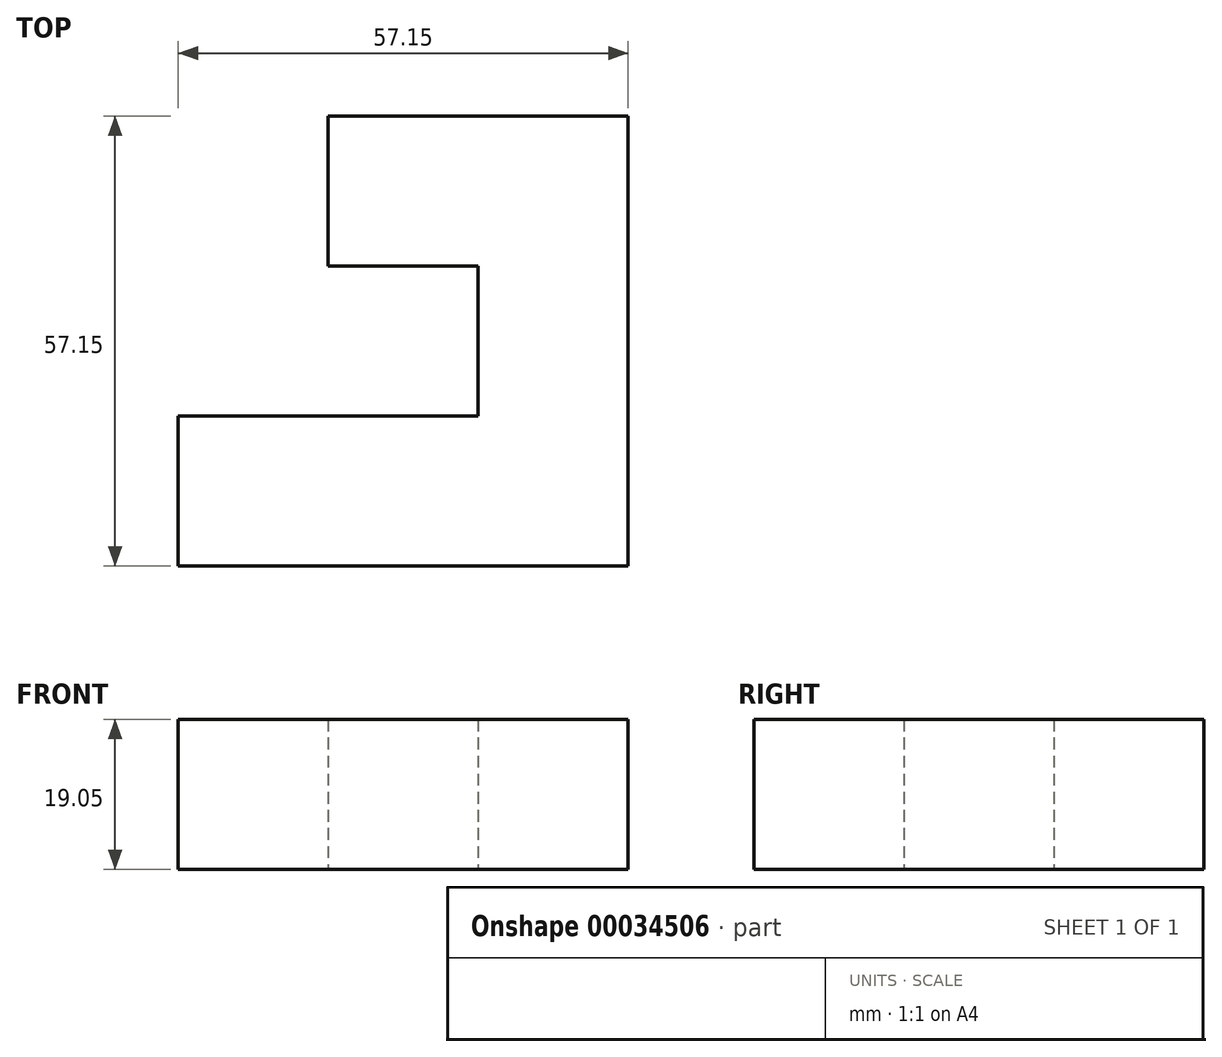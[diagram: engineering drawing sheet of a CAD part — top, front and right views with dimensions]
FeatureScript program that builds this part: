
annotation { "Feature Type Name" : "Feature", "Feature Type Description" : "" }
export const myFeature = defineFeature(function(context is Context, id is Id, definition is map)
    precondition{}
    {
        {
            var Q0;
            Q0=qCreatedBy(makeId("Top.planeOp"),FACE);
            var sketch = newSketch(context, id + "F0", { "sketchPlane" : qUnion([Q0])});
            skLineSegment(sketch, "E0.bottom", {"start": v(0, 0) * mm, "end": v(57.15, 0) * mm});
            skLineSegment(sketch, "E0.top", {"start": v(0, -19.05) * mm, "end": v(57.15, -19.05) * mm});
            skLineSegment(sketch, "E0.left", {"start": v(0, 0) * mm, "end": v(0, -19.05) * mm});
            skLineSegment(sketch, "E0.right", {"start": v(57.15, 0) * mm, "end": v(57.15, -19.05) * mm});
            skLineSegment(sketch, "E1.bottom", {"start": v(57.15, 0) * mm, "end": v(38.1, 0) * mm});
            skLineSegment(sketch, "E1.top", {"start": v(57.15, 38.1) * mm, "end": v(38.1, 38.1) * mm});
            skLineSegment(sketch, "E1.left", {"start": v(57.15, 0) * mm, "end": v(57.15, 38.1) * mm});
            skLineSegment(sketch, "E1.right", {"start": v(38.1, 0) * mm, "end": v(38.1, 38.1) * mm});
            skLineSegment(sketch, "E2.bottom", {"start": v(38.1, 38.1) * mm, "end": v(19.05, 38.1) * mm});
            skLineSegment(sketch, "E2.top", {"start": v(38.1, 19.05) * mm, "end": v(19.05, 19.05) * mm});
            skLineSegment(sketch, "E2.left", {"start": v(38.1, 38.1) * mm, "end": v(38.1, 19.05) * mm});
            skLineSegment(sketch, "E2.right", {"start": v(19.05, 38.1) * mm, "end": v(19.05, 19.05) * mm});
            skSolve(sketch);
        }
        {
            var Q0;
            Q0 = qSketchRegion(id + "F0", true);
            extrude(context, id + "F1", {"entities" : qUnion([Q0]), "depth" : 19.05 * mm});
        }
    });
